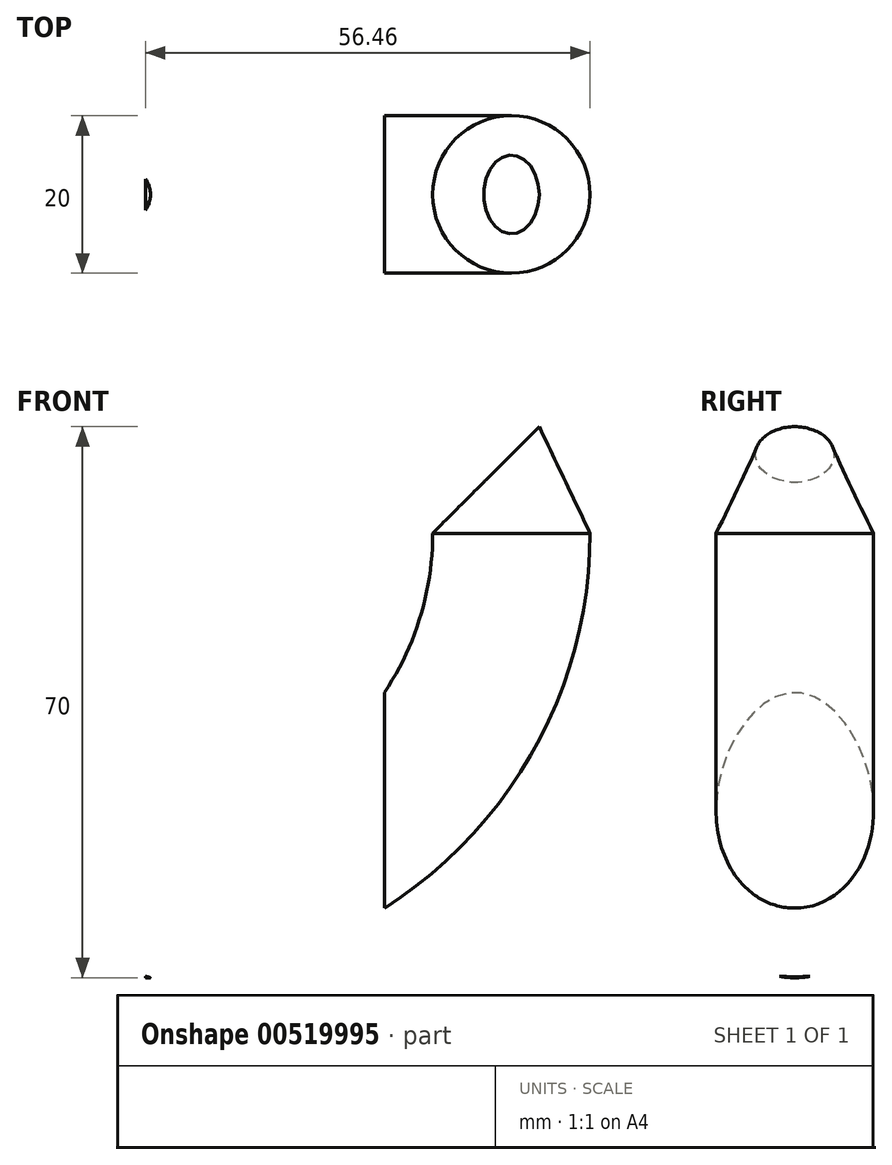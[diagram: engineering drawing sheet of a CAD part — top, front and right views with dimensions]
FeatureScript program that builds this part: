
annotation { "Feature Type Name" : "Feature", "Feature Type Description" : "" }
export const myFeature = defineFeature(function(context is Context, id is Id, definition is map)
    precondition{}
    {
        {
            var Q0;
            Q0=qCreatedBy(makeId("Front.planeOp"),FACE);
            var sketch = newSketch(context, id + "F0", { "sketchPlane" : qUnion([Q0])});
            skLineSegment(sketch, "E0", {"start": v(-94.46, 0) * mm, "end": v(-94.46, 100) * mm});
            skLineSegment(sketch, "E1", {"start": v(-94.46, 100) * mm, "end": v(5.54, 100) * mm});
            skLineSegment(sketch, "E2", {"start": v(5.54, 100) * mm, "end": v(5.54, 90) * mm});
            skLineSegment(sketch, "E3", {"start": v(5.54, 90) * mm, "end": v(-1.53, 82.93) * mm});
            skPoint(sketch, "E4", {"position": v(-94.46, 50) * mm});
            skLineSegment(sketch, "E5", {"start": v(-94.46, 70) * mm, "end": v(-94.46, 30) * mm});
            skPoint(sketch, "E6", {"position": v(2, 86.46) * mm});
            skLineSegment(sketch, "E7", {"start": v(2, 86.46) * mm, "end": v(2, 33.65) * mm});
            skPoint(sketch, "E8", {"position": v(2, 76.46) * mm});
            skLineSegment(sketch, "E9", {"start": v(-94.46, 30) * mm, "end": v(-44.46, 30) * mm});
            skLineSegment(sketch, "E10", {"start": v(11.06, 85.52) * mm, "end": v(-5.07, 69.4) * mm});
            skLineSegment(sketch, "E11", {"start": v(-5.07, 69.4) * mm, "end": v(-5.07, 30) * mm});
            skLineSegment(sketch, "E12", {"start": v(-44.46, 30) * mm, "end": v(16.2, 30) * mm});
            skPoint(sketch, "E13", {"position": v(-5.07, 51.4) * mm});
            skArc(sketch, "E14", {"start": v(-44.46, 30) * mm, "mid": v(-11.6, 43.6) * mm, "end": v(2, 76.46) * mm});
            skArc(sketch, "E15", {"start": v(-94.46, 30) * mm, "mid": v(-48.5, 35.42) * mm, "end": v(-5.07, 51.4) * mm});
            skSolve(sketch);
        }
        {
            var Q0;
            Q0=sQuery(id+"F0.wireOp",EDGE,"E3");
            cPlane(context, id + "F1", {"entities" : qUnion([Q0]), "cplaneType" : CPlaneType.LINE_ANGLE, "offset" : 25 * mm, "angle" : 90 * degree, "width" : 150 * mm, "height" : 150 * mm});
        }
        {
            var Q0;
            Q0=qCreatedBy(id+"F1.planeOp",FACE);
            var sketch = newSketch(context, id + "F2", { "sketchPlane" : qUnion([Q0])});
            skCircle(sketch, "E16", {"center": v(0, 62.56) * mm, "radius": 5 * mm});
            skSolve(sketch);
        }
        {
            var Q0;
            Q0=sQuery(id+"F0.wireOp",VERTEX,"E8");
            var Q1;
            Q1=qCreatedBy(makeId("Top.planeOp"),FACE);
            cPlane(context, id + "F3", {"entities" : qUnion([Q0, Q1]), "cplaneType" : CPlaneType.PLANE_POINT, "offset" : 25 * mm, "width" : 150 * mm, "height" : 150 * mm});
        }
        {
            var Q0;
            Q0=qCreatedBy(id+"F3.planeOp",FACE);
            var sketch = newSketch(context, id + "F4", { "sketchPlane" : qUnion([Q0])});
            skCircle(sketch, "E17", {"center": v(2, 0) * mm, "radius": 10 * mm});
            skPoint(sketch, "E18", {"position": v(0, -9.8) * mm});
            skSolve(sketch);
        }
        {
            var Q0;
            Q0=makeQuery(id+"F2.imprint","IMPRINT",FACE,{"disambiguationData":[TD([[makeQuery(id+"F2.imprint","IMPRINT",EDGE,{"derivedFrom":sQuery(id+"F2.wireOp",EDGE,"E16")}),1.0]])]});
            var Q1;
            Q1=makeQuery(id+"F4.imprint","IMPRINT",FACE,{"disambiguationData":[TD([[makeQuery(id+"F4.imprint","IMPRINT",EDGE,{"derivedFrom":sQuery(id+"F4.wireOp",EDGE,"E17")}),1.0]])]});
            loft(context, id + "F5", {"sheetProfilesArray" : [{ "sheetProfileEntities" : qUnion([Q0]) }, { "sheetProfileEntities" : qUnion([Q1]) }]});
        }
        {
            var Q0;
            Q0=makeQuery(id+"F4.imprint","IMPRINT",FACE,{"disambiguationData":[TD([[makeQuery(id+"F4.imprint","IMPRINT",EDGE,{"derivedFrom":sQuery(id+"F4.wireOp",EDGE,"E17")}),1.0]])]});
            var Q1;
            Q1=sQuery(id+"F0.wireOp",EDGE,"E14");
            sweep(context, id + "F6", {"operationType" : NewBodyOperationType.ADD, "profiles" : qUnion([Q0]), "path" : qUnion([Q1])});
        }
        {
            var Q0;
            Q0=sQuery(id+"F0.wireOp",EDGE,"E5");
            cPlane(context, id + "F7", {"entities" : qUnion([Q0]), "cplaneType" : CPlaneType.LINE_ANGLE, "offset" : 25 * mm, "angle" : 0 * degree, "width" : 150 * mm, "height" : 150 * mm});
        }
        {
            var Q0;
            Q0=qCreatedBy(id+"F7.planeOp",FACE);
            var sketch = newSketch(context, id + "F8", { "sketchPlane" : qUnion([Q0])});
            skCircle(sketch, "E19", {"center": v(0, 50) * mm, "radius": 20 * mm});
            skSolve(sketch);
        }
        {
            var Q0;
            Q0=sQuery(id+"F0.wireOp",EDGE,"E12");
            cPoint(context, id + "F9", {"entities" : qUnion([Q0]), "parameter" : 0.5});
        }
        {
            var Q0;
            Q0 = qCreatedBy(id + "F9" ,VERTEX);
            var Q1;
            Q1=qCreatedBy(id+"F7.planeOp",FACE);
            cPlane(context, id + "F10", {"entities" : qUnion([Q0, Q1]), "cplaneType" : CPlaneType.PLANE_POINT, "offset" : 25 * mm, "width" : 150 * mm, "height" : 150 * mm});
        }
        {
            var Q0;
            Q0=qCreatedBy(id+"F10.planeOp",FACE);
            var sketch = newSketch(context, id + "F11", { "sketchPlane" : qUnion([Q0])});
            skCircle(sketch, "E20", {"center": v(0, 48.23) * mm, "radius": 34.1 * mm});
            skPoint(sketch, "E21", {"position": v(0, 28.6) * mm});
            skSolve(sketch);
        }
        {
            var Q1;
            Q1=makeQuery(id+"F11.imprint","IMPRINT",FACE,{"disambiguationData":[TD([[makeQuery(id+"F11.imprint","IMPRINT",EDGE,{"derivedFrom":sQuery(id+"F11.wireOp",EDGE,"E20")}),1.0]])]});
            var Q2;
            Q2=makeQuery(id+"F8.imprint","IMPRINT",FACE,{"disambiguationData":[TD([[makeQuery(id+"F8.imprint","IMPRINT",EDGE,{"derivedFrom":sQuery(id+"F8.wireOp",EDGE,"E19")}),1.0]])]});
            loft(context, id + "F12", {"operationType" : NewBodyOperationType.REMOVE, "sheetProfilesArray" : [{ "sheetProfileEntities" : qUnion([Q1]) }, { "sheetProfileEntities" : qUnion([Q2]) }]});
        }
    });
